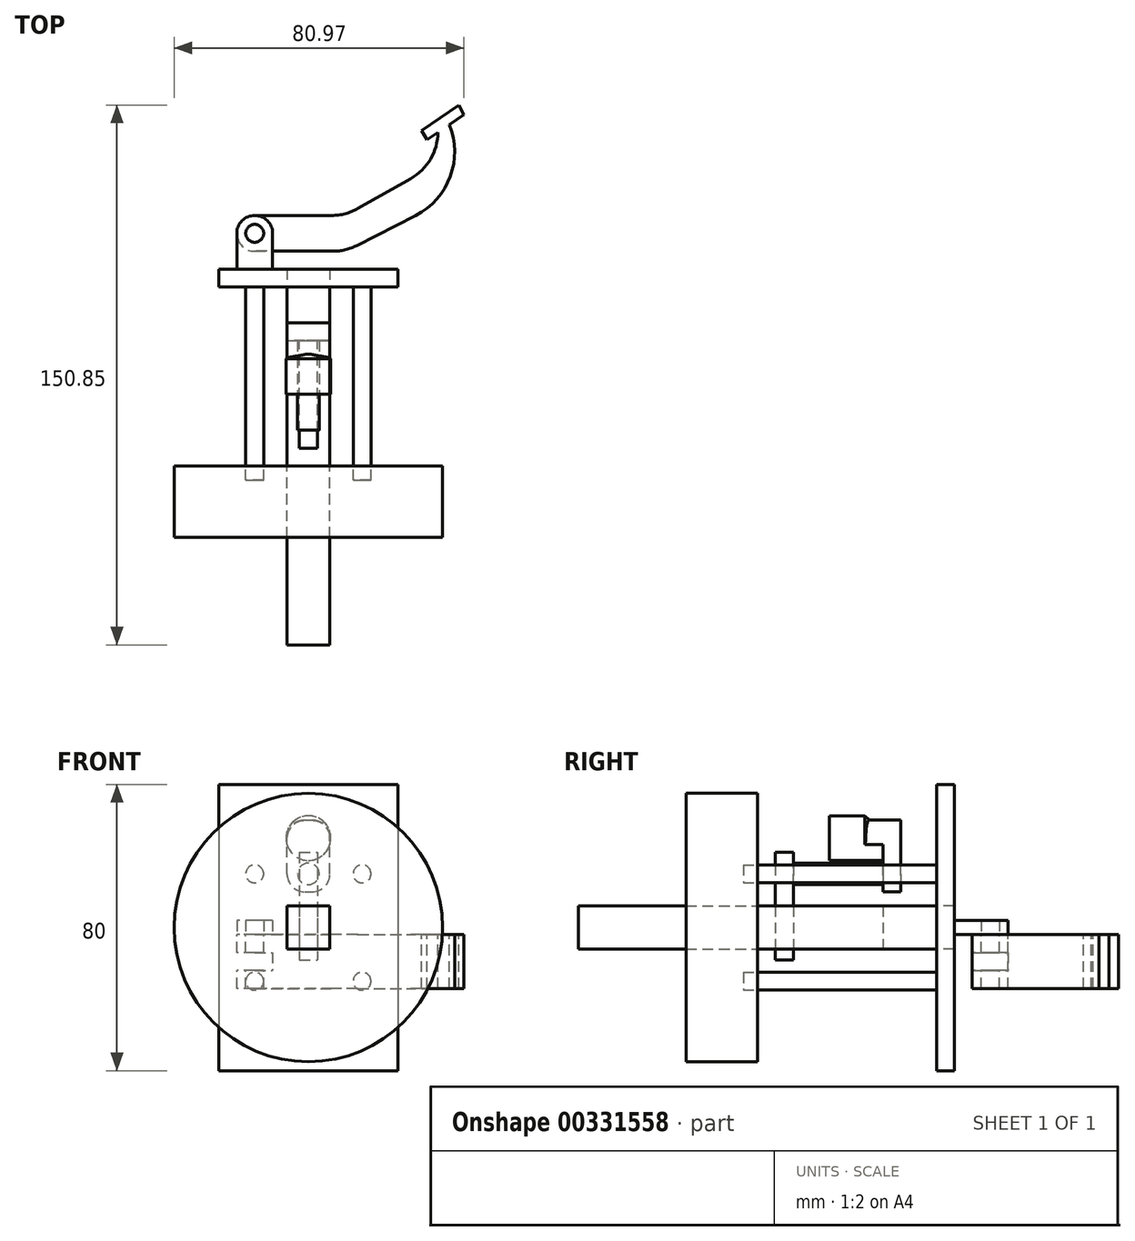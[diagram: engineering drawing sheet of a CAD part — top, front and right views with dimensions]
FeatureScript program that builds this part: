
annotation { "Feature Type Name" : "Feature", "Feature Type Description" : "" }
export const myFeature = defineFeature(function(context is Context, id is Id, definition is map)
    precondition{}
    {
        {
            var Q0;
            Q0=qCreatedBy(makeId("Right.planeOp"),FACE);
            var sketch = newSketch(context, id + "F0", { "sketchPlane" : qUnion([Q0])});
            skLineSegment(sketch, "E0.bottom", {"start": v(-2.5, 40) * mm, "end": v(2.5, 40) * mm});
            skLineSegment(sketch, "E0.top", {"start": v(-2.5, -40) * mm, "end": v(2.5, -40) * mm});
            skLineSegment(sketch, "E0.left", {"start": v(-2.5, 40) * mm, "end": v(-2.5, -40) * mm});
            skLineSegment(sketch, "E0.right", {"start": v(2.5, 40) * mm, "end": v(2.5, -40) * mm});
            skSolve(sketch);
        }
        {
            var Q0;
            Q0=makeQuery(id+"F0.imprint","IMPRINT",FACE,{"disambiguationData":[TD([[makeQuery(id+"F0.imprint","IMPRINT",EDGE,{"derivedFrom":sQuery(id+"F0.wireOp",EDGE,"E0.bottom")}),-1.0]])]});
            extrude(context, id + "F1", {"entities" : qUnion([Q0]), "depth" : 50 * mm});
        }
        {
            var Q0;
            Q0=makeQuery(id+"F1.opExtrude","SWEPT_FACE",FACE,{"disambiguationData":[OSD([sQuery(id+"F0.wireOp",EDGE,"E0.left")])]});
            var sketch = newSketch(context, id + "F2", { "sketchPlane" : qUnion([Q0])});
            skLineSegment(sketch, "E1.bottom", {"start": v(31, 6) * mm, "end": v(19, 6) * mm});
            skLineSegment(sketch, "E1.top", {"start": v(31, -6) * mm, "end": v(19, -6) * mm});
            skLineSegment(sketch, "E1.left", {"start": v(31, 6) * mm, "end": v(31, -6) * mm});
            skLineSegment(sketch, "E1.right", {"start": v(19, 6) * mm, "end": v(19, -6) * mm});
            skPoint(sketch, "E1.middle", {"position": v(25, 0) * mm});
            skSolve(sketch);
        }
        {
            var Q0;
            Q0=makeQuery(id+"F2.imprint","IMPRINT",FACE,{"disambiguationData":[TD([[makeQuery(id+"F2.imprint","IMPRINT",EDGE,{"derivedFrom":sQuery(id+"F2.wireOp",EDGE,"E1.bottom")}),1.0]])]});
            extrude(context, id + "F3", {"entities" : qUnion([Q0]), "operationType" : NewBodyOperationType.REMOVE, "oppositeDirection" : true, "depth" : 25 * mm});
        }
        {
            var Q0;
            Q0=makeQuery(id+"F2.imprint","IMPRINT",FACE,{"disambiguationData":[TD([[makeQuery(id+"F2.imprint","IMPRINT",EDGE,{"derivedFrom":sQuery(id+"F2.wireOp",EDGE,"E1.bottom")}),1.0]])]});
            extrude(context, id + "F4", {"entities" : qUnion([Q0]), "depth" : 50 * mm});
        }
        {
            var Q0;
            Q0=makeQuery(id+"F4.opExtrude","CAP_FACE",FACE,{"disambiguationData":[OSD([sQuery(id+"F2.wireOp",EDGE,"E1.bottom"),sQuery(id+"F2.wireOp",EDGE,"E1.top"),sQuery(id+"F2.wireOp",EDGE,"E1.left"),sQuery(id+"F2.wireOp",EDGE,"E1.right")])],"isStart":false});
            extrude(context, id + "F5", {"entities" : qUnion([Q0]), "depth" : 50 * mm});
        }
        {
            var Q0;
            Q0=makeQuery(id+"F4.opExtrude","SWEPT_FACE",FACE,{"disambiguationData":[OSD([sQuery(id+"F2.wireOp",EDGE,"E1.top")])]});
            var sketch = newSketch(context, id + "F6", { "sketchPlane" : qUnion([Q0])});
            skLineSegment(sketch, "E2.bottom", {"start": v(27.5, 47.5) * mm, "end": v(22.5, 47.5) * mm});
            skLineSegment(sketch, "E2.top", {"start": v(27.5, 17.5) * mm, "end": v(22.5, 17.5) * mm});
            skLineSegment(sketch, "E2.left", {"start": v(27.5, 47.5) * mm, "end": v(27.5, 17.5) * mm});
            skLineSegment(sketch, "E2.right", {"start": v(22.5, 47.5) * mm, "end": v(22.5, 17.5) * mm});
            skPoint(sketch, "E2.middle", {"position": v(25, 32.5) * mm});
            skSolve(sketch);
        }
        {
            var Q0;
            Q0=makeQuery(id+"F6.imprint","IMPRINT",FACE,{"disambiguationData":[TD([[makeQuery(id+"F6.imprint","IMPRINT",EDGE,{"derivedFrom":sQuery(id+"F6.wireOp",EDGE,"E2.bottom")}),1.0]])]});
            extrude(context, id + "F7", {"entities" : qUnion([Q0]), "operationType" : NewBodyOperationType.REMOVE, "oppositeDirection" : true, "depth" : 25 * mm});
        }
        {
            var Q0;
            Q0=makeQuery(id+"F4.opExtrude","SWEPT_FACE",FACE,{"disambiguationData":[OSD([sQuery(id+"F2.wireOp",EDGE,"E1.bottom")])]});
            var sketch = newSketch(context, id + "F8", { "sketchPlane" : qUnion([Q0])});
            skLineSegment(sketch, "E3.bottom", {"start": v(22.5, -47.5) * mm, "end": v(27.5, -47.5) * mm});
            skLineSegment(sketch, "E3.top", {"start": v(22.5, -42.5) * mm, "end": v(27.5, -42.5) * mm});
            skLineSegment(sketch, "E3.left", {"start": v(22.5, -47.5) * mm, "end": v(22.5, -42.5) * mm});
            skLineSegment(sketch, "E3.right", {"start": v(27.5, -47.5) * mm, "end": v(27.5, -42.5) * mm});
            skPoint(sketch, "E3.middle", {"position": v(25, -45) * mm});
            skSolve(sketch);
        }
        {
            var Q0;
            Q0=makeQuery(id+"F8.imprint","IMPRINT",FACE,{"disambiguationData":[TD([[makeQuery(id+"F8.imprint","IMPRINT",EDGE,{"derivedFrom":sQuery(id+"F8.wireOp",EDGE,"E3.bottom")}),-1.0]])]});
            extrude(context, id + "F9", {"entities" : qUnion([Q0]), "depth" : 15 * mm, "hasSecondDirection" : true, "secondDirectionOppositeDirection" : true, "secondDirectionDepth" : 15 * mm});
        }
        {
            var Q0;
            Q0=makeQuery(id+"F9.opExtrude","SWEPT_FACE",FACE,{"disambiguationData":[OSD([sQuery(id+"F8.wireOp",EDGE,"E3.top")])]});
            var sketch = newSketch(context, id + "F10", { "sketchPlane" : qUnion([Q0])});
            skCircle(sketch, "E4", {"center": v(-25, 15) * mm, "radius": 3 * mm});
            skSolve(sketch);
        }
        {
            var Q0;
            Q0 = qSketchRegion(id + "F10", true);
            extrude(context, id + "F11", {"entities" : qUnion([Q0]), "depth" : 25 * mm});
        }
        {
            var Q0;
            Q0=makeQuery(id+"F11.opExtrude","CAP_FACE",FACE,{"disambiguationData":[OSD([sQuery(id+"F10.wireOp",EDGE,"E4")])],"isStart":false});
            var sketch = newSketch(context, id + "F12", { "sketchPlane" : qUnion([Q0])});
            skLineSegment(sketch, "E5.bottom", {"start": v(-19, 10) * mm, "end": v(-31, 10) * mm});
            skLineSegment(sketch, "E5.top", {"start": v(-19, 30) * mm, "end": v(-31, 30) * mm});
            skLineSegment(sketch, "E5.left", {"start": v(-19, 10) * mm, "end": v(-19, 30) * mm});
            skLineSegment(sketch, "E5.right", {"start": v(-31, 10) * mm, "end": v(-31, 30) * mm});
            skSolve(sketch);
        }
        {
            var Q0;
            Q0 = qSketchRegion(id + "F12", true);
            extrude(context, id + "F13", {"entities" : qUnion([Q0]), "operationType" : NewBodyOperationType.ADD, "depth" : 5 * mm});
        }
        {
            var Q0;
            Q0=makeQuery(id+"F13.opExtrude","SWEPT_EDGE",EDGE,{"disambiguationData":[OSD([sQuery(id+"F12.wireOp",EDGE,"E5.top"),sQuery(id+"F12.wireOp",EDGE,"E5.left")])]});
            var Q1;
            Q1=makeQuery(id+"F13.opExtrude","SWEPT_EDGE",EDGE,{"disambiguationData":[OSD([sQuery(id+"F12.wireOp",EDGE,"E5.top"),sQuery(id+"F12.wireOp",EDGE,"E5.right")])]});
            var Q2;
            Q2=makeQuery(id+"F13.opExtrude","SWEPT_EDGE",EDGE,{"disambiguationData":[OSD([sQuery(id+"F12.wireOp",EDGE,"E5.bottom"),sQuery(id+"F12.wireOp",EDGE,"E5.right")])]});
            var Q3;
            Q3=makeQuery(id+"F13.opExtrude","SWEPT_EDGE",EDGE,{"disambiguationData":[OSD([sQuery(id+"F12.wireOp",EDGE,"E5.bottom"),sQuery(id+"F12.wireOp",EDGE,"E5.left")])]});
            fillet(context, id + "F14", {"entities" : qUnion([Q0, Q1, Q2, Q3]), "radius" : 5 * mm, "tangentPropagation" : true, "allowEdgeOverflow" : false});
        }
        {
            var Q0;
            Q0=makeQuery(id+"F13.opExtrude","CAP_FACE",FACE,{"disambiguationData":[OSD([sQuery(id+"F12.wireOp",EDGE,"E5.bottom"),sQuery(id+"F12.wireOp",EDGE,"E5.top"),sQuery(id+"F12.wireOp",EDGE,"E5.left"),sQuery(id+"F12.wireOp",EDGE,"E5.right")])],"isStart":true});
            var sketch = newSketch(context, id + "F15", { "sketchPlane" : qUnion([Q0])});
            skCircle(sketch, "E6", {"center": v(25, 25) * mm, "radius": 6.25 * mm});
            skSolve(sketch);
        }
        {
            var Q0;
            Q0 = qSketchRegion(id + "F15", true);
            extrude(context, id + "F16", {"entities" : qUnion([Q0]), "operationType" : NewBodyOperationType.ADD, "depth" : 15 * mm});
        }
        {
            var Q0;
            {var subQ0=sQuery(id+"F15.wireOp",EDGE,"E6");Q0=makeQuery(id+"F16.boolean.opBoolean","SPLIT",EDGE,{"disambiguationData":[topologyDisambiguationEdgeConnected([makeQuery(id+"F16.opExtrude","CAP_FACE",FACE,{"disambiguationData":[OSD([subQ0])],"isStart":true})])],"derivedFrom":makeQuery(id+"F16.opExtrude","CAP_EDGE",EDGE,{"disambiguationData":[OSD([subQ0])],"isStart":true})});}
            chamfer(context, id + "F17", {"entities" : qUnion([Q0]), "width" : 5 * mm, "tangentPropagation" : true});
        }
        {
            var Q0;
            Q0=qCreatedBy(makeId("Top.planeOp"),FACE);
            var sketch = newSketch(context, id + "F18", { "sketchPlane" : qUnion([Q0])});
            skLineSegment(sketch, "E7.bottom", {"start": v(15, 2.5) * mm, "end": v(5, 2.5) * mm});
            skLineSegment(sketch, "E7.top", {"start": v(15, 12.5) * mm, "end": v(5, 12.5) * mm});
            skLineSegment(sketch, "E7.left", {"start": v(15, 2.5) * mm, "end": v(15, 12.5) * mm});
            skLineSegment(sketch, "E7.right", {"start": v(5, 2.5) * mm, "end": v(5, 12.5) * mm});
            skArc(sketch, "E8", {"start": v(15, 12.5) * mm, "mid": v(10, 17.5) * mm, "end": v(5, 12.5) * mm});
            skCircle(sketch, "E9", {"center": v(10, 12.5) * mm, "radius": 2.5 * mm});
            skSolve(sketch);
        }
        {
            var Q0;
            Q0 = qSketchRegion(id + "F18", true);
            extrude(context, id + "F19", {"entities" : qUnion([Q0]), "operationType" : NewBodyOperationType.ADD, "depth" : 2 * mm, "hasSecondDirection" : true, "secondDirectionOppositeDirection" : true, "secondDirectionDepth" : 2 * mm});
        }
        {
            var Q0;
            Q0=makeQuery(id+"F19.opExtrude","CAP_FACE",FACE,{"disambiguationData":[OSD([sQuery(id+"F18.wireOp",EDGE,"E7.bottom"),sQuery(id+"F18.wireOp",EDGE,"E7.left"),sQuery(id+"F18.wireOp",EDGE,"E7.right"),sQuery(id+"F18.wireOp",EDGE,"E8"),sQuery(id+"F18.wireOp",EDGE,"E9")])],"isStart":true});
            var sketch = newSketch(context, id + "F20", { "sketchPlane" : qUnion([Q0])});
            skCircle(sketch, "E10", {"center": v(10, -12.5) * mm, "radius": 2.5 * mm});
            skCircle(sketch, "E11", {"center": v(10, -12.5) * mm, "radius": 5 * mm});
            skLineSegment(sketch, "E12", {"start": v(10, -17.5) * mm, "end": v(31.45, -17.5) * mm});
            skPoint(sketch, "E12.endSnap0", {"position": v(10, -17.5) * mm});
            skLineSegment(sketch, "E13", {"start": v(35.41, -17.5) * mm, "end": v(35.41, -7.5) * mm});
            skPoint(sketch, "E13.endSnap0", {"position": v(15, -7.5) * mm});
            skLineSegment(sketch, "E14", {"start": v(31.8, -7.5) * mm, "end": v(10, -7.5) * mm});
            skLineSegment(sketch, "E15", {"start": v(38.85, -19.45) * mm, "end": v(53.58, -27.8) * mm});
            skLineSegment(sketch, "E16", {"start": v(38.63, -9.14) * mm, "end": v(54.97, -17.5) * mm});
            skPoint(sketch, "E17.visualSharp", {"position": v(35.41, -17.5) * mm});
            skArc(sketch, "E17.filletArc", {"start": v(38.85, -19.45) * mm, "mid": v(35.28, -18) * mm, "end": v(31.45, -17.5) * mm});
            skPoint(sketch, "E18.visualSharp", {"position": v(35.41, -7.5) * mm});
            skArc(sketch, "E18.filletArc", {"start": v(38.63, -9.14) * mm, "mid": v(35.3, -7.92) * mm, "end": v(31.8, -7.5) * mm});
            skArc(sketch, "E19", {"start": v(64.37, -42.9) * mm, "mid": v(64.62, -28.37) * mm, "end": v(54.97, -17.5) * mm});
            skArc(sketch, "E20", {"start": v(61.19, -40.73) * mm, "mid": v(59.12, -33.25) * mm, "end": v(53.58, -27.8) * mm});
            skLineSegment(sketch, "E21", {"start": v(58.1, -38.62) * mm, "end": v(68.47, -45.7) * mm});
            skLineSegment(sketch, "E22", {"start": v(58.1, -38.62) * mm, "end": v(56.66, -41.27) * mm});
            skLineSegment(sketch, "E23", {"start": v(68.47, -45.7) * mm, "end": v(67.04, -48.35) * mm});
            skLineSegment(sketch, "E24", {"start": v(56.66, -41.27) * mm, "end": v(67.04, -48.35) * mm});
            skSolve(sketch);
        }
        {
            var Q0;
            Q0 = qSketchRegion(id + "F20", true);
            extrude(context, id + "F21", {"entities" : qUnion([Q0]), "depth" : 15 * mm});
        }
        {
            var Q0;
            Q0=makeQuery(id+"F21.opExtrude","SWEPT_FACE",FACE,{"disambiguationData":[OSD([sQuery(id+"F20.wireOp",EDGE,"E12")])]});
            var sketch = newSketch(context, id + "F22", { "sketchPlane" : qUnion([Q0])});
            skLineSegment(sketch, "E25.bottom", {"start": v(0, -7) * mm, "end": v(-15, -7) * mm});
            skLineSegment(sketch, "E25.top", {"start": v(0, -12) * mm, "end": v(-15, -12) * mm});
            skLineSegment(sketch, "E25.left", {"start": v(0, -7) * mm, "end": v(0, -12) * mm});
            skLineSegment(sketch, "E25.right", {"start": v(-15, -7) * mm, "end": v(-15, -12) * mm});
            skSolve(sketch);
        }
        {
            var Q0;
            Q0 = qSketchRegion(id + "F22", true);
            extrude(context, id + "F23", {"entities" : qUnion([Q0]), "operationType" : NewBodyOperationType.REMOVE, "oppositeDirection" : true, "depth" : 10 * mm});
        }
        {
            var Q0;
            Q0=makeQuery(id+"F5.opExtrude","CAP_FACE",FACE,{"disambiguationData":[OSD([sQuery(id+"F2.wireOp",EDGE,"E1.bottom"),sQuery(id+"F2.wireOp",EDGE,"E1.top"),sQuery(id+"F2.wireOp",EDGE,"E1.left"),sQuery(id+"F2.wireOp",EDGE,"E1.right")])],"isStart":true});
            var sketch = newSketch(context, id + "F24", { "sketchPlane" : qUnion([Q0])});
            skCircle(sketch, "E26", {"center": v(-25, 0) * mm, "radius": 37.5 * mm});
            skSolve(sketch);
        }
        {
            var Q0;
            Q0=makeQuery(id+"F24.imprint","IMPRINT",FACE,{"disambiguationData":[TD([[makeQuery(id+"F24.imprint","IMPRINT",EDGE,{"derivedFrom":sQuery(id+"F24.wireOp",EDGE,"E26")}),1.0]])]});
            extrude(context, id + "F25", {"entities" : qUnion([Q0]), "oppositeDirection" : true, "depth" : 20 * mm});
        }
        {
            var Q0;
            {var subQ0=sQuery(id+"F2.wireOp",EDGE,"E1.right");var subQ1=sQuery(id+"F2.wireOp",EDGE,"E1.left");var subQ2=sQuery(id+"F2.wireOp",EDGE,"E1.top");var subQ3=sQuery(id+"F2.wireOp",EDGE,"E1.bottom");Q0=makeQuery(id+"F25.boolean.opBoolean","MERGE",FACE,{"derivedFrom":[makeQuery(id+"F5.opExtrude","CAP_FACE",FACE,{"disambiguationData":[OSD([subQ3,subQ2,subQ1,subQ0])],"isStart":true}),makeQuery(id+"F25.opExtrude","CAP_FACE",FACE,{"disambiguationData":[OSD([subQ3,subQ2,subQ1,subQ0,sQuery(id+"F24.wireOp",EDGE,"E26")])],"isStart":true})]});}
            var sketch = newSketch(context, id + "F26", { "sketchPlane" : qUnion([Q0])});
            skCircle(sketch, "E27", {"center": v(-40, 15) * mm, "radius": 2.5 * mm});
            skCircle(sketch, "E28", {"center": v(-10, 15) * mm, "radius": 2.5 * mm});
            skLineSegment(sketch, "E29", {"start": v(0, 0) * mm, "end": v(-46.78, 0) * mm, "construction": true});
            skCircle(sketch, "E30.MirrorC", {"center": v(-40, -15) * mm, "radius": 2.5 * mm});
            skCircle(sketch, "E31.MirrorC", {"center": v(-10, -15) * mm, "radius": 2.5 * mm});
            skSolve(sketch);
        }
        {
            var Q0;
            Q0 = qSketchRegion(id + "F26", true);
            extrude(context, id + "F27", {"entities" : qUnion([Q0]), "depth" : 50 * mm});
        }
        {
            var Q0;
            Q0 = qSketchRegion(id + "F26", true);
            extrude(context, id + "F28", {"entities" : qUnion([Q0]), "operationType" : NewBodyOperationType.REMOVE, "oppositeDirection" : true, "depth" : 4 * mm});
        }
    });
